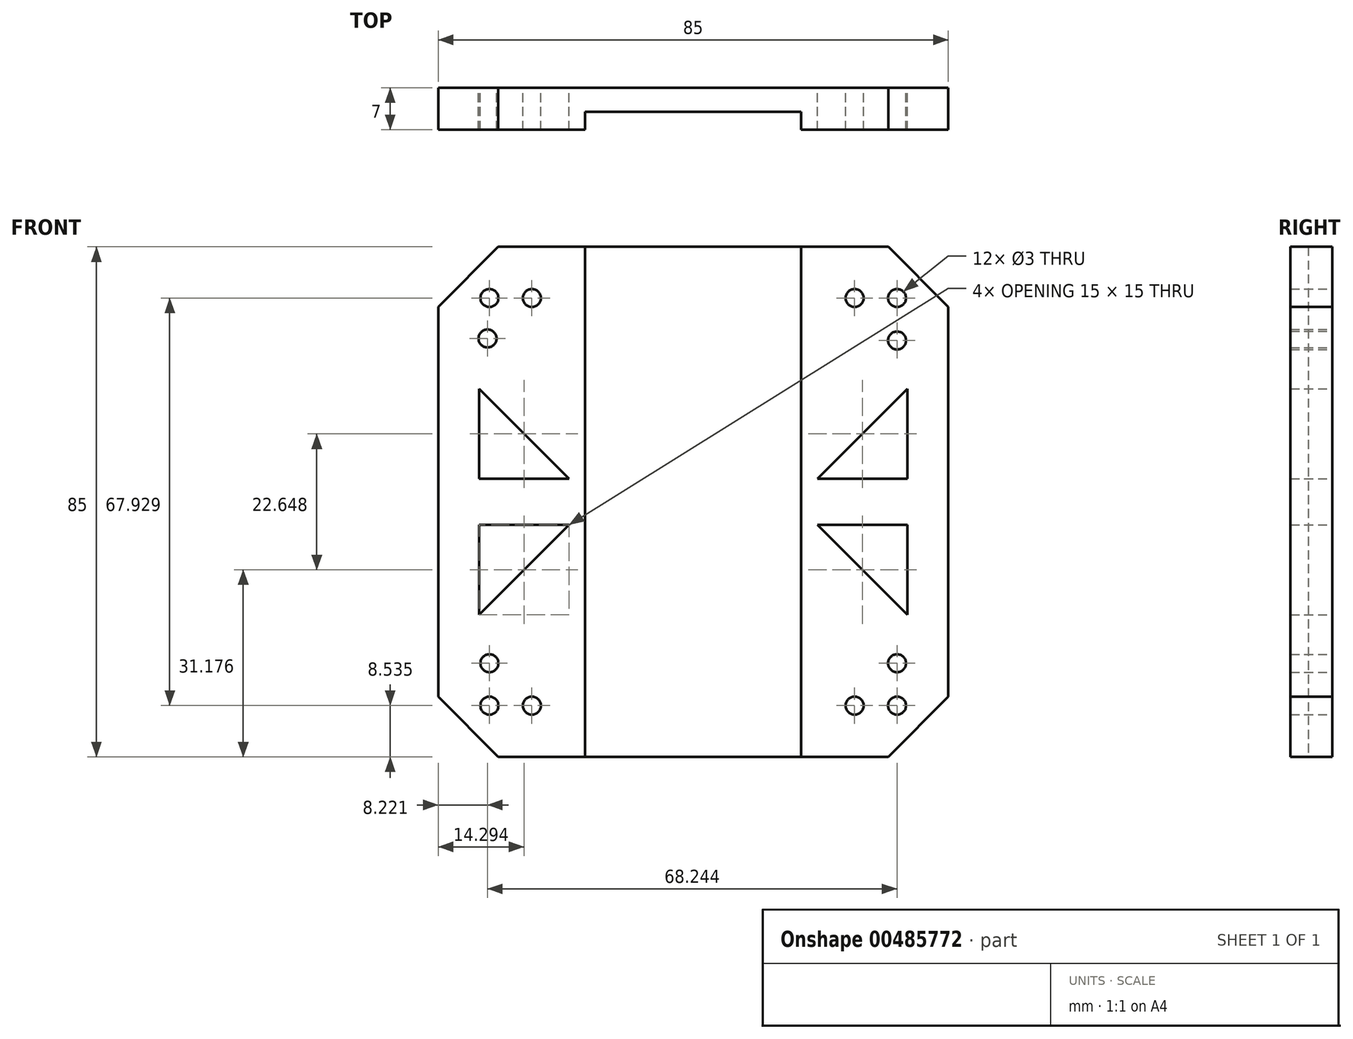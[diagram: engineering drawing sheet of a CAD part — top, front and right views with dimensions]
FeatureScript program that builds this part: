
annotation { "Feature Type Name" : "Feature", "Feature Type Description" : "" }
export const myFeature = defineFeature(function(context is Context, id is Id, definition is map)
    precondition{}
    {
        {
            var Q0;
            Q0=qCreatedBy(makeId("Front.planeOp"),FACE);
            var sketch = newSketch(context, id + "F0", { "sketchPlane" : qUnion([Q0])});
            skLineSegment(sketch, "E0.left", {"start": v(42.5, 42.5) * mm, "end": v(42.5, -42.5) * mm});
            skLineSegment(sketch, "E0.right", {"start": v(-42.5, 42.5) * mm, "end": v(-42.5, -42.5) * mm});
            skPoint(sketch, "E0.middle", {"position": v(0, 0) * mm});
            skLineSegment(sketch, "E1", {"start": v(-42.5, 32.5) * mm, "end": v(-32.5, 42.5) * mm});
            skLineSegment(sketch, "E2", {"start": v(-42.5, 42.5) * mm, "end": v(-30.34, 30.34) * mm});
            skCircle(sketch, "E3", {"center": v(-33.96, 33.96) * mm, "radius": 1.5 * mm});
            skCircle(sketch, "E4", {"center": v(-34.28, 27.22) * mm, "radius": 1.5 * mm});
            skCircle(sketch, "E5", {"center": v(-26.9, 33.96) * mm, "radius": 1.5 * mm});
            skLineSegment(sketch, "E6", {"start": v(-34.28, 27.22) * mm, "end": v(-26.9, 33.96) * mm});
            skLineSegment(sketch, "E7", {"start": v(32.5, 42.5) * mm, "end": v(42.5, 32.5) * mm});
            skLineSegment(sketch, "E8", {"start": v(42.5, 42.5) * mm, "end": v(25.43, 25.43) * mm});
            skCircle(sketch, "E9", {"center": v(33.96, 33.96) * mm, "radius": 1.5 * mm});
            skPoint(sketch, "E9.centerSnap0", {"position": v(33.96, 33.96) * mm});
            skCircle(sketch, "E10", {"center": v(26.9, 33.96) * mm, "radius": 1.5 * mm});
            skCircle(sketch, "E11", {"center": v(33.96, 26.9) * mm, "radius": 1.5 * mm});
            skLineSegment(sketch, "E12", {"start": v(42.5, -32.5) * mm, "end": v(32.5, -42.5) * mm});
            skLineSegment(sketch, "E13", {"start": v(42.5, -42.5) * mm, "end": v(26.16, -26.16) * mm});
            skCircle(sketch, "E14", {"center": v(33.96, -33.96) * mm, "radius": 1.5 * mm});
            skCircle(sketch, "E15", {"center": v(33.96, -26.9) * mm, "radius": 1.5 * mm});
            skCircle(sketch, "E16", {"center": v(26.9, -33.96) * mm, "radius": 1.5 * mm});
            skLineSegment(sketch, "E17", {"start": v(26.9, 33.96) * mm, "end": v(33.96, 26.9) * mm});
            skLineSegment(sketch, "E18", {"start": v(-42.5, -32.5) * mm, "end": v(-32.5, -42.5) * mm});
            skLineSegment(sketch, "E19", {"start": v(-42.5, -42.5) * mm, "end": v(-26, -26) * mm});
            skCircle(sketch, "E20", {"center": v(-33.96, -33.96) * mm, "radius": 1.5 * mm});
            skCircle(sketch, "E21", {"center": v(-26.9, -33.96) * mm, "radius": 1.5 * mm});
            skCircle(sketch, "E22", {"center": v(-33.96, -26.9) * mm, "radius": 1.5 * mm});
            skLineSegment(sketch, "E23", {"start": v(-35.7, 18.82) * mm, "end": v(-35.7, 3.82) * mm});
            skLineSegment(sketch, "E24", {"start": v(-35.7, 3.82) * mm, "end": v(-20.7, 3.82) * mm});
            skLineSegment(sketch, "E25", {"start": v(-20.7, 3.82) * mm, "end": v(-35.7, 18.82) * mm});
            skLineSegment(sketch, "E26.MirrorCS", {"start": v(-35.7, -18.82) * mm, "end": v(-35.7, -3.82) * mm});
            skLineSegment(sketch, "E27.MirrorCS", {"start": v(-20.7, -3.82) * mm, "end": v(-35.7, -18.82) * mm});
            skLineSegment(sketch, "E28.MirrorCS", {"start": v(-35.7, -3.82) * mm, "end": v(-20.7, -3.82) * mm});
            skLineSegment(sketch, "E29.MirrorCS", {"start": v(20.7, 3.82) * mm, "end": v(35.7, 18.82) * mm});
            skLineSegment(sketch, "E30.MirrorCS", {"start": v(35.7, 3.82) * mm, "end": v(20.7, 3.82) * mm});
            skLineSegment(sketch, "E31.MirrorCS", {"start": v(35.7, 18.82) * mm, "end": v(35.7, 3.82) * mm});
            skLineSegment(sketch, "E32.MirrorCS", {"start": v(35.7, -3.82) * mm, "end": v(20.7, -3.82) * mm});
            skLineSegment(sketch, "E33.MirrorCS", {"start": v(20.7, -3.82) * mm, "end": v(35.7, -18.82) * mm});
            skLineSegment(sketch, "E34.MirrorCS", {"start": v(35.7, -18.82) * mm, "end": v(35.7, -3.82) * mm});
            skLineSegment(sketch, "E35", {"start": v(-42.5, 42.5) * mm, "end": v(42.5, 42.5) * mm});
            skLineSegment(sketch, "E36", {"start": v(-42.5, -42.5) * mm, "end": v(42.5, -42.5) * mm});
            skLineSegment(sketch, "E37", {"start": v(-18, -42.5) * mm, "end": v(-18, 42.5) * mm});
            skLineSegment(sketch, "E38", {"start": v(18, -42.5) * mm, "end": v(18, 42.5) * mm});
            skSolve(sketch);
        }
        {
            var Q0;
            Q0 = qSketchRegion(id + "F0", true);
            extrude(context, id + "F1", {"entities" : qUnion([Q0]), "depth" : 4 * mm, "offsetDistance" : 25 * mm});
        }
        {
            var Q0;
            Q0=makeQuery(id+"F1.opExtrude","SWEPT_EDGE",EDGE,{"disambiguationData":[OSD([sQuery(id+"F0.wireOp",EDGE,"E0.bottom"),sQuery(id+"F0.wireOp",EDGE,"E0.left")])]});
            var Q1;
            Q1=makeQuery(id+"F1.opExtrude","SWEPT_EDGE",EDGE,{"disambiguationData":[OSD([sQuery(id+"F0.wireOp",EDGE,"E0.bottom"),sQuery(id+"F0.wireOp",EDGE,"E0.right")])]});
            var Q2;
            Q2=makeQuery(id+"F1.opExtrude","SWEPT_EDGE",EDGE,{"disambiguationData":[OSD([sQuery(id+"F0.wireOp",EDGE,"E0.top"),sQuery(id+"F0.wireOp",EDGE,"E0.right")])]});
            var Q3;
            Q3=makeQuery(id+"F1.opExtrude","SWEPT_EDGE",EDGE,{"disambiguationData":[OSD([sQuery(id+"F0.wireOp",EDGE,"E0.top"),sQuery(id+"F0.wireOp",EDGE,"E0.left")])]});
            chamfer(context, id + "F2", {"entities" : qUnion([Q0, Q1, Q2, Q3]), "width" : 10 * mm, "tangentPropagation" : true});
        }
        {
            var Q0;
            Q0=makeQuery(id+"F0.imprint","IMPRINT",FACE,{"disambiguationData":[TD([[makeQuery(id+"F0.imprint","IMPRINT",EDGE,{"derivedFrom":sQuery(id+"F0.wireOp",EDGE,"E4")}),-1.0]])]});
            var Q1;
            Q1=makeQuery(id+"F0.imprint","IMPRINT",FACE,{"disambiguationData":[TD([[makeQuery(id+"F0.imprint","IMPRINT",EDGE,{"derivedFrom":sQuery(id+"F0.wireOp",EDGE,"E10")}),-1.0]])]});
            extrude(context, id + "F3", {"entities" : qUnion([Q0, Q1]), "operationType" : NewBodyOperationType.ADD, "depth" : 7 * mm, "offsetDistance" : 25 * mm});
        }
    });
